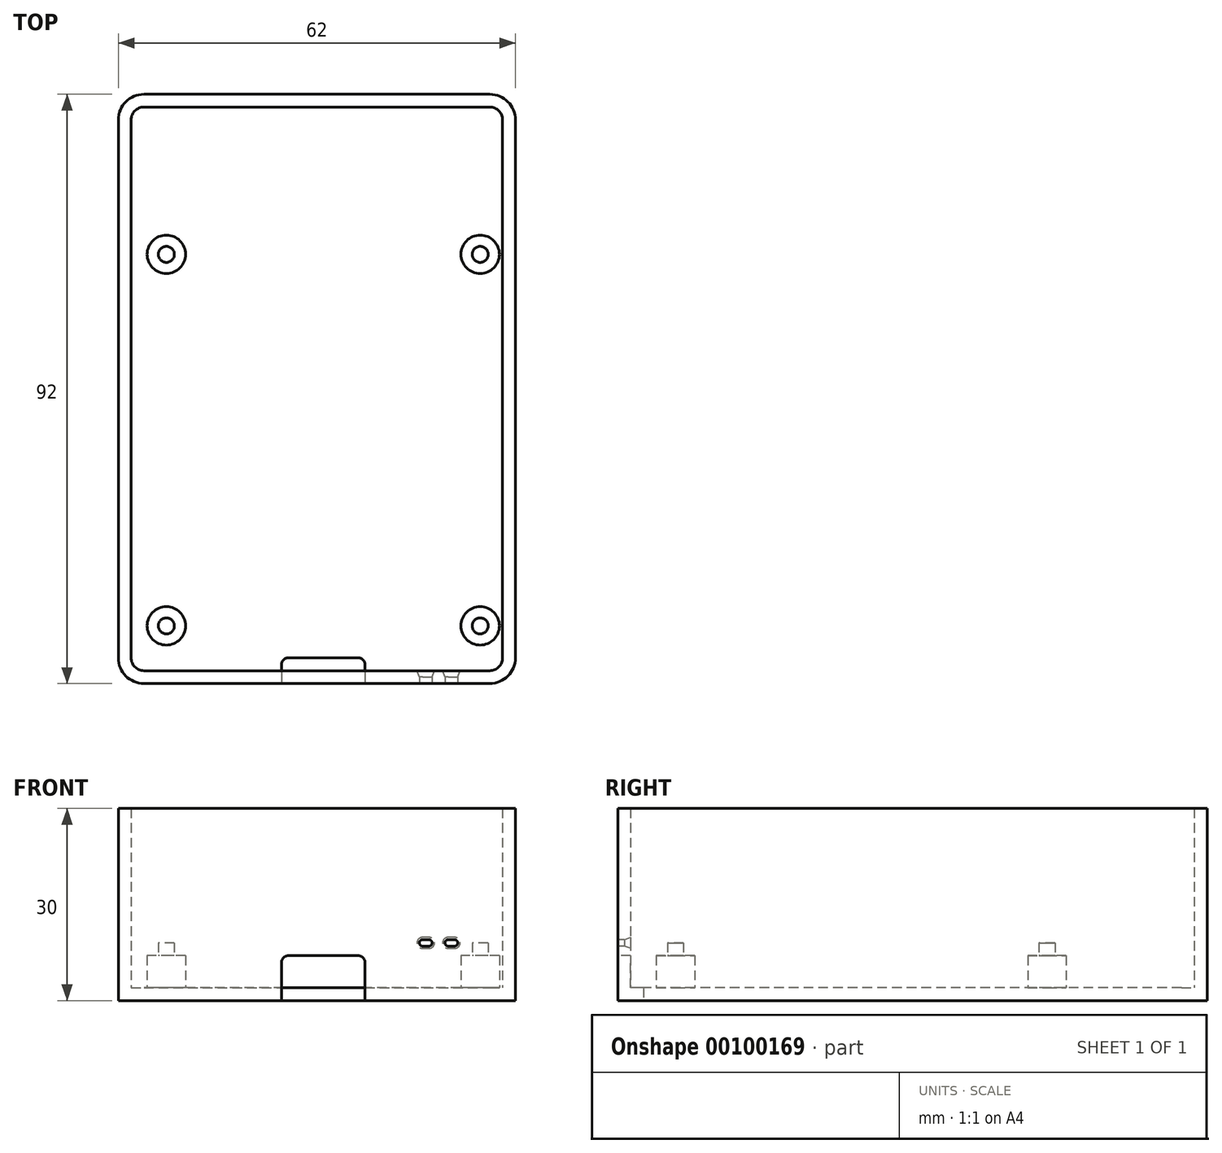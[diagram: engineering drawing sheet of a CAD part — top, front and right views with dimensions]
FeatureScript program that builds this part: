
annotation { "Feature Type Name" : "Feature", "Feature Type Description" : "" }
export const myFeature = defineFeature(function(context is Context, id is Id, definition is map)
    precondition{}
    {
        {
            var Q0;
            Q0=qCreatedBy(makeId("Top.planeOp"),FACE);
            var sketch = newSketch(context, id + "F0", { "sketchPlane" : qUnion([Q0])});
            skLineSegment(sketch, "E0.bottom", {"start": v(62, 0) * mm, "end": v(0, 0) * mm});
            skLineSegment(sketch, "E0.top", {"start": v(62, 92) * mm, "end": v(0, 92) * mm});
            skLineSegment(sketch, "E0.left", {"start": v(62, 0) * mm, "end": v(62, 92) * mm});
            skLineSegment(sketch, "E0.right", {"start": v(0, 0) * mm, "end": v(0, 92) * mm});
            skSolve(sketch);
        }
        {
            var Q0;
            Q0=makeQuery(id+"F0.imprint","IMPRINT",FACE,{"disambiguationData":[TD([[makeQuery(id+"F0.imprint","IMPRINT",EDGE,{"derivedFrom":sQuery(id+"F0.wireOp",EDGE,"E0.bottom")}),-1.0]])]});
            extrude(context, id + "F1", {"entities" : qUnion([Q0]), "depth" : 2 * mm});
        }
        {
            var Q0;
            Q0=makeQuery(id+"F1.opExtrude","CAP_FACE",FACE,{"disambiguationData":[OSD([sQuery(id+"F0.wireOp",EDGE,"E0.bottom"),sQuery(id+"F0.wireOp",EDGE,"E0.top"),sQuery(id+"F0.wireOp",EDGE,"E0.left"),sQuery(id+"F0.wireOp",EDGE,"E0.right")])],"isStart":false});
            var sketch = newSketch(context, id + "F2", { "sketchPlane" : qUnion([Q0])});
            skLineSegment(sketch, "E1.0", {"start": v(2, 2) * mm, "end": v(60, 2) * mm});
            skLineSegment(sketch, "E1.1", {"start": v(2, 90) * mm, "end": v(2, 2) * mm});
            skLineSegment(sketch, "E1.2", {"start": v(60, 90) * mm, "end": v(2, 90) * mm});
            skLineSegment(sketch, "E1.3", {"start": v(60, 2) * mm, "end": v(60, 90) * mm});
            skLineSegment(sketch, "E2.bottom", {"start": v(7.5, 67) * mm, "end": v(56.5, 67) * mm, "construction": true});
            skLineSegment(sketch, "E2.top", {"start": v(7.5, 9) * mm, "end": v(56.5, 9) * mm, "construction": true});
            skLineSegment(sketch, "E2.left", {"start": v(7.5, 67) * mm, "end": v(7.5, 9) * mm, "construction": true});
            skLineSegment(sketch, "E2.right", {"start": v(56.5, 67) * mm, "end": v(56.5, 9) * mm, "construction": true});
            skCircle(sketch, "E3", {"center": v(7.5, 67) * mm, "radius": 3 * mm});
            skCircle(sketch, "E4", {"center": v(56.5, 67) * mm, "radius": 3 * mm});
            skCircle(sketch, "E5", {"center": v(56.5, 9) * mm, "radius": 3 * mm});
            skCircle(sketch, "E6", {"center": v(7.5, 9) * mm, "radius": 3 * mm});
            skSolve(sketch);
        }
        {
            var Q0;
            Q0=makeQuery(id+"F2.imprint","IMPRINT",FACE,{"disambiguationData":[TD([[makeQuery(id+"F2.imprint","IMPRINT",EDGE,{"derivedFrom":sQuery(id+"F2.wireOp",EDGE,"E1.0")}),-1.0]])]});
            var Q1;
            Q1=makeQuery(id+"F2.imprint","IMPRINT",FACE,{"disambiguationData":[TD([[makeQuery(id+"F2.imprint","IMPRINT",EDGE,{"derivedFrom":sQuery(id+"F2.wireOp",EDGE,"E3")}),1.0]])]});
            var Q2;
            Q2=makeQuery(id+"F2.imprint","IMPRINT",FACE,{"disambiguationData":[TD([[makeQuery(id+"F2.imprint","IMPRINT",EDGE,{"derivedFrom":sQuery(id+"F2.wireOp",EDGE,"E4")}),1.0]])]});
            var Q3;
            Q3=makeQuery(id+"F2.imprint","IMPRINT",FACE,{"disambiguationData":[TD([[makeQuery(id+"F2.imprint","IMPRINT",EDGE,{"derivedFrom":sQuery(id+"F2.wireOp",EDGE,"E6")}),1.0]])]});
            var Q4;
            Q4=makeQuery(id+"F2.imprint","IMPRINT",FACE,{"disambiguationData":[TD([[makeQuery(id+"F2.imprint","IMPRINT",EDGE,{"derivedFrom":sQuery(id+"F2.wireOp",EDGE,"E5")}),1.0]])]});
            extrude(context, id + "F3", {"entities" : qUnion([Q0, Q1, Q2, Q3, Q4]), "operationType" : NewBodyOperationType.ADD, "depth" : 28 * mm});
        }
        {
            var Q0;
            Q0=makeQuery(id+"F3.opExtrude","CAP_FACE",FACE,{"disambiguationData":[OSD([sQuery(id+"F2.wireOp",EDGE,"E3")])],"isStart":false});
            var Q1;
            Q1=makeQuery(id+"F3.opExtrude","CAP_FACE",FACE,{"disambiguationData":[OSD([sQuery(id+"F2.wireOp",EDGE,"E4")])],"isStart":false});
            var Q2;
            Q2=makeQuery(id+"F3.opExtrude","CAP_FACE",FACE,{"disambiguationData":[OSD([sQuery(id+"F2.wireOp",EDGE,"E5")])],"isStart":false});
            var Q3;
            Q3=makeQuery(id+"F3.opExtrude","CAP_FACE",FACE,{"disambiguationData":[OSD([sQuery(id+"F2.wireOp",EDGE,"E6")])],"isStart":false});
            extrude(context, id + "F4", {"entities" : qUnion([Q0, Q1, Q2, Q3]), "operationType" : NewBodyOperationType.REMOVE, "oppositeDirection" : true, "depth" : 23 * mm});
        }
        {
            var Q0;
            Q0=makeQuery(id+"F4.boolean.opBoolean","COPY",FACE,{"derivedFrom":makeQuery(id+"F4.opExtrude","CAP_FACE",FACE,{"disambiguationData":[OSD([sQuery(id+"F2.wireOp",EDGE,"E6")])],"isStart":false})});
            var sketch = newSketch(context, id + "F5", { "sketchPlane" : qUnion([Q0])});
            skCircle(sketch, "E7", {"center": v(7.5, 9) * mm, "radius": 1.25 * mm});
            skSolve(sketch);
        }
        {
            var Q0;
            Q0 = qSketchRegion(id + "F5", true);
            extrude(context, id + "F6", {"entities" : qUnion([Q0]), "operationType" : NewBodyOperationType.ADD, "depth" : 2 * mm});
        }
        {
            var Q0;
            Q0=makeQuery(id+"F4.boolean.opBoolean","COPY",FACE,{"derivedFrom":makeQuery(id+"F4.opExtrude","CAP_FACE",FACE,{"disambiguationData":[OSD([sQuery(id+"F2.wireOp",EDGE,"E5")])],"isStart":false})});
            var sketch = newSketch(context, id + "F7", { "sketchPlane" : qUnion([Q0])});
            skCircle(sketch, "E8", {"center": v(56.5, 9) * mm, "radius": 1.25 * mm});
            skSolve(sketch);
        }
        {
            var Q0;
            Q0 = qSketchRegion(id + "F7", true);
            extrude(context, id + "F8", {"entities" : qUnion([Q0]), "operationType" : NewBodyOperationType.ADD, "depth" : 2 * mm});
        }
        {
            var Q0;
            Q0=makeQuery(id+"F4.boolean.opBoolean","COPY",FACE,{"derivedFrom":makeQuery(id+"F4.opExtrude","CAP_FACE",FACE,{"disambiguationData":[OSD([sQuery(id+"F2.wireOp",EDGE,"E4")])],"isStart":false})});
            var sketch = newSketch(context, id + "F9", { "sketchPlane" : qUnion([Q0])});
            skCircle(sketch, "E9", {"center": v(56.5, 67) * mm, "radius": 1.25 * mm});
            skSolve(sketch);
        }
        {
            var Q0;
            Q0 = qSketchRegion(id + "F9", true);
            extrude(context, id + "F10", {"entities" : qUnion([Q0]), "operationType" : NewBodyOperationType.ADD, "depth" : 2 * mm});
        }
        {
            var Q0;
            Q0=makeQuery(id+"F4.boolean.opBoolean","COPY",FACE,{"derivedFrom":makeQuery(id+"F4.opExtrude","CAP_FACE",FACE,{"disambiguationData":[OSD([sQuery(id+"F2.wireOp",EDGE,"E3")])],"isStart":false})});
            var sketch = newSketch(context, id + "F11", { "sketchPlane" : qUnion([Q0])});
            skCircle(sketch, "E10", {"center": v(7.5, 67) * mm, "radius": 1.25 * mm});
            skSolve(sketch);
        }
        {
            var Q0;
            Q0 = qSketchRegion(id + "F11", true);
            extrude(context, id + "F12", {"entities" : qUnion([Q0]), "operationType" : NewBodyOperationType.ADD, "depth" : 2 * mm});
        }
        {
            var Q0;
            {var subQ0=sQuery(id+"F0.wireOp",EDGE,"E0.bottom");Q0=makeQuery(id+"F3.boolean.opBoolean","MERGE",FACE,{"derivedFrom":[makeQuery(id+"F1.opExtrude","SWEPT_FACE",FACE,{"disambiguationData":[OSD([subQ0])]}),makeQuery(id+"F3.opExtrude","SWEPT_FACE",FACE,{"disambiguationData":[OSD([subQ0])]})]});}
            var sketch = newSketch(context, id + "F13", { "sketchPlane" : qUnion([Q0])});
            skLineSegment(sketch, "E11.bottom", {"start": v(51.5, 9.5) * mm, "end": v(52.5, 9.5) * mm});
            skLineSegment(sketch, "E11.top", {"start": v(51.5, 8.5) * mm, "end": v(52.5, 8.5) * mm});
            skLineSegment(sketch, "E11.left", {"start": v(51, 9) * mm, "end": v(51, 9) * mm});
            skLineSegment(sketch, "E11.right", {"start": v(53, 9) * mm, "end": v(53, 9) * mm});
            skLineSegment(sketch, "E12.bottom", {"start": v(47.5, 9.5) * mm, "end": v(48.5, 9.5) * mm});
            skLineSegment(sketch, "E12.top", {"start": v(47.5, 8.5) * mm, "end": v(48.5, 8.5) * mm});
            skLineSegment(sketch, "E12.left", {"start": v(47, 9) * mm, "end": v(47, 9) * mm});
            skLineSegment(sketch, "E12.right", {"start": v(49, 9) * mm, "end": v(49, 9) * mm});
            skLineSegment(sketch, "E13", {"start": v(56.5, 9.01) * mm, "end": v(56.5, 6.99) * mm, "construction": true});
            skLineSegment(sketch, "E14", {"start": v(52.63, 7) * mm, "end": v(33.92, 7) * mm, "construction": true});
            skLineSegment(sketch, "E15.bottom", {"start": v(37.5, 7) * mm, "end": v(26.5, 7) * mm});
            skLineSegment(sketch, "E15.top", {"start": v(38.5, 0) * mm, "end": v(25.5, 0) * mm});
            skLineSegment(sketch, "E15.left", {"start": v(38.5, 6) * mm, "end": v(38.5, 0) * mm});
            skLineSegment(sketch, "E15.right", {"start": v(25.5, 6) * mm, "end": v(25.5, 0) * mm});
            skPoint(sketch, "E16.visualSharp", {"position": v(25.5, 7) * mm});
            skArc(sketch, "E16.filletArc", {"start": v(26.5, 7) * mm, "mid": v(25.8, 6.7) * mm, "end": v(25.5, 6) * mm});
            skPoint(sketch, "E17.visualSharp", {"position": v(38.5, 7) * mm});
            skArc(sketch, "E17.filletArc", {"start": v(38.5, 6) * mm, "mid": v(38.2, 6.7) * mm, "end": v(37.5, 7) * mm});
            skPoint(sketch, "E18.visualSharp", {"position": v(47, 9.5) * mm});
            skArc(sketch, "E18.filletArc", {"start": v(47.5, 9.5) * mm, "mid": v(47.15, 9.35) * mm, "end": v(47, 9) * mm});
            skPoint(sketch, "E19.visualSharp", {"position": v(49, 9.5) * mm});
            skArc(sketch, "E19.filletArc", {"start": v(49, 9) * mm, "mid": v(48.85, 9.35) * mm, "end": v(48.5, 9.5) * mm});
            skPoint(sketch, "E20.visualSharp", {"position": v(49, 8.5) * mm});
            skArc(sketch, "E20.filletArc", {"start": v(48.5, 8.5) * mm, "mid": v(48.85, 8.65) * mm, "end": v(49, 9) * mm});
            skPoint(sketch, "E21.visualSharp", {"position": v(47, 8.5) * mm});
            skArc(sketch, "E21.filletArc", {"start": v(47, 9) * mm, "mid": v(47.15, 8.65) * mm, "end": v(47.5, 8.5) * mm});
            skPoint(sketch, "E22.visualSharp", {"position": v(51, 9.5) * mm});
            skArc(sketch, "E22.filletArc", {"start": v(51.5, 9.5) * mm, "mid": v(51.15, 9.35) * mm, "end": v(51, 9) * mm});
            skPoint(sketch, "E23.visualSharp", {"position": v(53, 9.5) * mm});
            skArc(sketch, "E23.filletArc", {"start": v(53, 9) * mm, "mid": v(52.85, 9.35) * mm, "end": v(52.5, 9.5) * mm});
            skPoint(sketch, "E24.visualSharp", {"position": v(53, 8.5) * mm});
            skArc(sketch, "E24.filletArc", {"start": v(52.5, 8.5) * mm, "mid": v(52.85, 8.65) * mm, "end": v(53, 9) * mm});
            skPoint(sketch, "E25.visualSharp", {"position": v(51, 8.5) * mm});
            skArc(sketch, "E25.filletArc", {"start": v(51, 9) * mm, "mid": v(51.15, 8.65) * mm, "end": v(51.5, 8.5) * mm});
            skSolve(sketch);
        }
        {
            var Q0;
            Q0=makeQuery(id+"F13.imprint","IMPRINT",FACE,{"disambiguationData":[TD([[makeQuery(id+"F13.imprint","IMPRINT",EDGE,{"derivedFrom":sQuery(id+"F13.wireOp",EDGE,"E15.bottom")}),1.0]])]});
            var Q1;
            Q1=makeQuery(id+"F13.imprint","IMPRINT",FACE,{"disambiguationData":[TD([[makeQuery(id+"F13.imprint","IMPRINT",EDGE,{"derivedFrom":sQuery(id+"F13.wireOp",EDGE,"E12.bottom")}),-1.0]])]});
            var Q2;
            Q2=makeQuery(id+"F13.imprint","IMPRINT",FACE,{"disambiguationData":[TD([[makeQuery(id+"F13.imprint","IMPRINT",EDGE,{"derivedFrom":sQuery(id+"F13.wireOp",EDGE,"E11.bottom")}),-1.0]])]});
            extrude(context, id + "F14", {"entities" : qUnion([Q0, Q1, Q2]), "operationType" : NewBodyOperationType.REMOVE, "oppositeDirection" : true, "depth" : 4 * mm});
        }
        {
            var Q0;
            Q0=makeQuery(id+"F14.boolean.opBoolean","COPY",EDGE,{"derivedFrom":makeQuery(id+"F14.opExtrude","CAP_EDGE",EDGE,{"disambiguationData":[OSD([sQuery(id+"F13.wireOp",EDGE,"E15.right")])],"isStart":false})});
            var Q1;
            Q1=makeQuery(id+"F14.boolean.opBoolean","COPY",EDGE,{"derivedFrom":makeQuery(id+"F14.opExtrude","CAP_EDGE",EDGE,{"disambiguationData":[OSD([sQuery(id+"F13.wireOp",EDGE,"E15.left")])],"isStart":false})});
            fillet(context, id + "F15", {"entities" : qUnion([Q0, Q1]), "radius" : 1 * mm, "tangentPropagation" : true, "allowEdgeOverflow" : false});
        }
        {
            var Q0;
            Q0=makeQuery(id+"F3.opExtrude","SWEPT_EDGE",EDGE,{"disambiguationData":[OSD([sQuery(id+"F2.wireOp",EDGE,"E1.1"),sQuery(id+"F2.wireOp",EDGE,"E1.2")])]});
            var Q1;
            Q1=makeQuery(id+"F3.opExtrude","SWEPT_EDGE",EDGE,{"disambiguationData":[OSD([sQuery(id+"F2.wireOp",EDGE,"E1.2"),sQuery(id+"F2.wireOp",EDGE,"E1.3")])]});
            var Q2;
            Q2=makeQuery(id+"F3.opExtrude","SWEPT_EDGE",EDGE,{"disambiguationData":[OSD([sQuery(id+"F2.wireOp",EDGE,"E1.0"),sQuery(id+"F2.wireOp",EDGE,"E1.3")])]});
            var Q3;
            Q3=makeQuery(id+"F3.opExtrude","SWEPT_EDGE",EDGE,{"disambiguationData":[OSD([sQuery(id+"F2.wireOp",EDGE,"E1.0"),sQuery(id+"F2.wireOp",EDGE,"E1.1")])]});
            fillet(context, id + "F16", {"entities" : qUnion([Q0, Q1, Q2, Q3]), "radius" : 2 * mm, "tangentPropagation" : true, "allowEdgeOverflow" : false});
        }
        {
            var Q0;
            {var subQ0=sQuery(id+"F0.wireOp",EDGE,"E0.right");var subQ1=sQuery(id+"F0.wireOp",EDGE,"E0.top");Q0=makeQuery(id+"F3.boolean.opBoolean","MERGE",EDGE,{"derivedFrom":[makeQuery(id+"F1.opExtrude","SWEPT_EDGE",EDGE,{"disambiguationData":[OSD([subQ1,subQ0])]}),makeQuery(id+"F3.opExtrude","SWEPT_EDGE",EDGE,{"disambiguationData":[OSD([subQ1,subQ0])]})]});}
            var Q1;
            {var subQ0=sQuery(id+"F0.wireOp",EDGE,"E0.left");var subQ1=sQuery(id+"F0.wireOp",EDGE,"E0.top");Q1=makeQuery(id+"F3.boolean.opBoolean","MERGE",EDGE,{"derivedFrom":[makeQuery(id+"F1.opExtrude","SWEPT_EDGE",EDGE,{"disambiguationData":[OSD([subQ1,subQ0])]}),makeQuery(id+"F3.opExtrude","SWEPT_EDGE",EDGE,{"disambiguationData":[OSD([subQ1,subQ0])]})]});}
            var Q2;
            {var subQ0=sQuery(id+"F0.wireOp",EDGE,"E0.left");var subQ1=sQuery(id+"F0.wireOp",EDGE,"E0.bottom");Q2=makeQuery(id+"F3.boolean.opBoolean","MERGE",EDGE,{"derivedFrom":[makeQuery(id+"F1.opExtrude","SWEPT_EDGE",EDGE,{"disambiguationData":[OSD([subQ1,subQ0])]}),makeQuery(id+"F3.opExtrude","SWEPT_EDGE",EDGE,{"disambiguationData":[OSD([subQ1,subQ0])]})]});}
            var Q3;
            {var subQ0=sQuery(id+"F0.wireOp",EDGE,"E0.right");var subQ1=sQuery(id+"F0.wireOp",EDGE,"E0.bottom");Q3=makeQuery(id+"F3.boolean.opBoolean","MERGE",EDGE,{"derivedFrom":[makeQuery(id+"F1.opExtrude","SWEPT_EDGE",EDGE,{"disambiguationData":[OSD([subQ1,subQ0])]}),makeQuery(id+"F3.opExtrude","SWEPT_EDGE",EDGE,{"disambiguationData":[OSD([subQ1,subQ0])]})]});}
            fillet(context, id + "F17", {"entities" : qUnion([Q0, Q1, Q2, Q3]), "radius" : 4 * mm, "tangentPropagation" : true, "allowEdgeOverflow" : false});
        }
        {
            var Q0;
            Q0=makeQuery(id+"F14.boolean.opBoolean","INTERSECT",EDGE,{"derivedFrom":[makeQuery(id+"F3.opExtrude","SWEPT_FACE",FACE,{"disambiguationData":[OSD([sQuery(id+"F2.wireOp",EDGE,"E1.0")])]}),makeQuery(id+"F14.opExtrude","SWEPT_FACE",FACE,{"disambiguationData":[OSD([sQuery(id+"F13.wireOp",EDGE,"E22.filletArc"),sQuery(id+"F13.wireOp",EDGE,"E25.filletArc")])]})]});
            var Q1;
            Q1=makeQuery(id+"F14.boolean.opBoolean","INTERSECT",EDGE,{"derivedFrom":[makeQuery(id+"F3.opExtrude","SWEPT_FACE",FACE,{"disambiguationData":[OSD([sQuery(id+"F2.wireOp",EDGE,"E1.0")])]}),makeQuery(id+"F14.opExtrude","SWEPT_FACE",FACE,{"disambiguationData":[OSD([sQuery(id+"F13.wireOp",EDGE,"E18.filletArc"),sQuery(id+"F13.wireOp",EDGE,"E21.filletArc")])]})]});
            chamfer(context, id + "F18", {"entities" : qUnion([Q0, Q1]), "chamferType" : ChamferType.OFFSET_ANGLE, "width" : 1 * mm, "oppositeDirection" : false, "angle" : 20 * degree, "tangentPropagation" : true});
        }
    });
